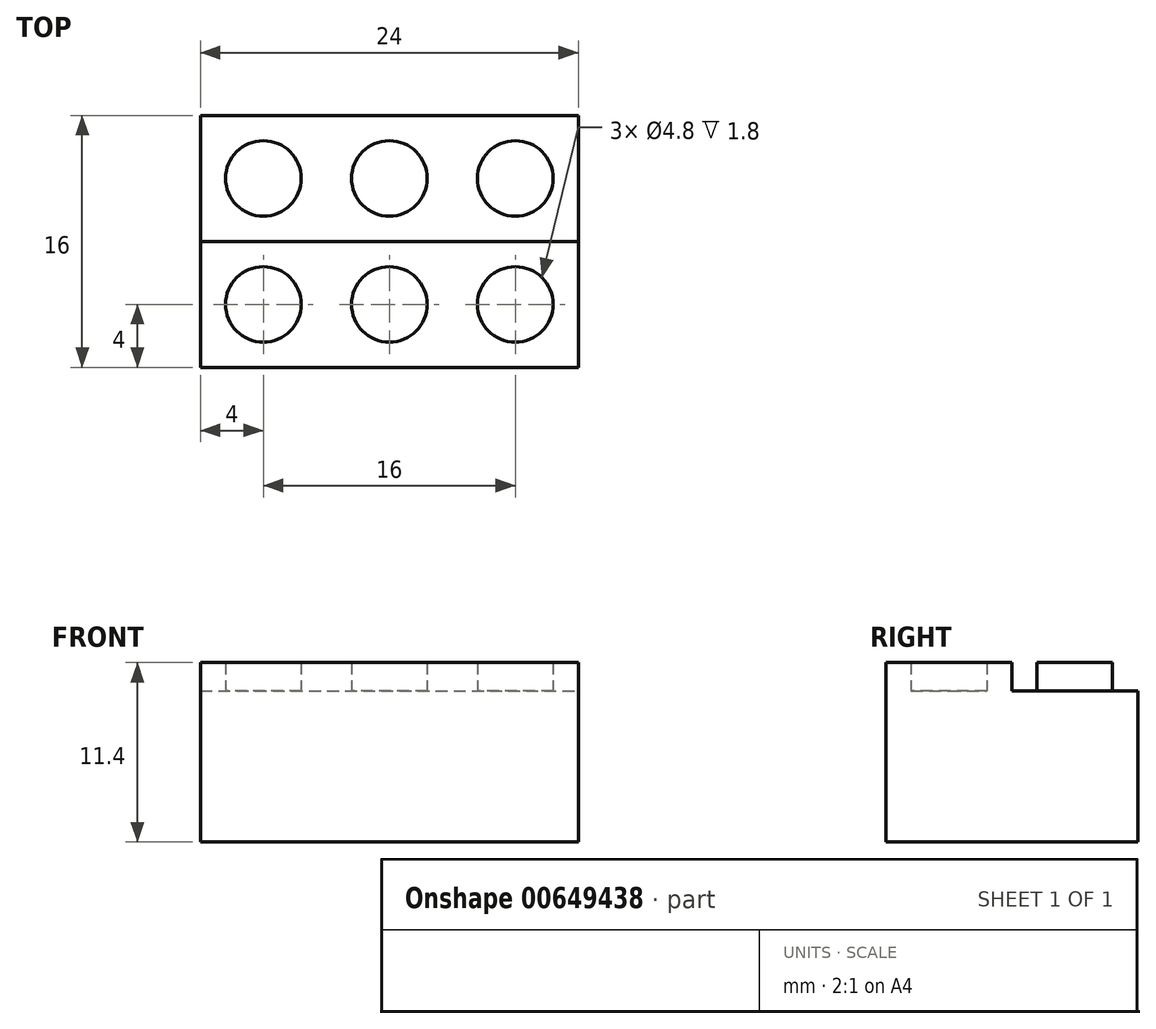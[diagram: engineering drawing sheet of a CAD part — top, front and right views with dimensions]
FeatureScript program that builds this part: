
annotation { "Feature Type Name" : "Feature", "Feature Type Description" : "" }
export const myFeature = defineFeature(function(context is Context, id is Id, definition is map)
    precondition{}
    {
        {
            var Q0;
            Q0=qCreatedBy(makeId("Top.planeOp"),FACE);
            var sketch = newSketch(context, id + "F0", { "sketchPlane" : qUnion([Q0])});
            skLineSegment(sketch, "E0.bottom", {"start": v(0, 0) * mm, "end": v(-24, 0) * mm});
            skLineSegment(sketch, "E0.top", {"start": v(0, 16) * mm, "end": v(-24, 16) * mm});
            skLineSegment(sketch, "E0.left", {"start": v(0, 0) * mm, "end": v(0, 16) * mm});
            skLineSegment(sketch, "E0.right", {"start": v(-24, 0) * mm, "end": v(-24, 16) * mm});
            skSolve(sketch);
        }
        {
            var Q0;
            Q0=makeQuery(id+"F0.imprint","IMPRINT",FACE,{"disambiguationData":[TD([[makeQuery(id+"F0.imprint","IMPRINT",EDGE,{"derivedFrom":sQuery(id+"F0.wireOp",EDGE,"E0.bottom")}),-1.0]])]});
            extrude(context, id + "F1", {"entities" : qUnion([Q0]), "depth" : 9.6 * mm, "offsetDistance" : 25.4 * mm});
        }
        {
            var Q0;
            Q0=makeQuery(id+"F1.opExtrude","CAP_FACE",FACE,{"disambiguationData":[OSD([sQuery(id+"F0.wireOp",EDGE,"E0.bottom"),sQuery(id+"F0.wireOp",EDGE,"E0.top"),sQuery(id+"F0.wireOp",EDGE,"E0.left"),sQuery(id+"F0.wireOp",EDGE,"E0.right")])],"isStart":false});
            var sketch = newSketch(context, id + "F2", { "sketchPlane" : qUnion([Q0])});
            skLineSegment(sketch, "E1", {"start": v(-24, 8) * mm, "end": v(0, 8) * mm});
            skLineSegment(sketch, "E2", {"start": v(-16, 16) * mm, "end": v(-16, 0) * mm});
            skLineSegment(sketch, "E3", {"start": v(-8, 16) * mm, "end": v(-8, 0) * mm});
            skCircle(sketch, "E4", {"center": v(-20, 12) * mm, "radius": 2.4 * mm});
            skCircle(sketch, "E5", {"center": v(-12, 12) * mm, "radius": 2.4 * mm});
            skCircle(sketch, "E6", {"center": v(-4, 12) * mm, "radius": 2.4 * mm});
            skCircle(sketch, "E7.MirrorC", {"center": v(-20, 4) * mm, "radius": 2.4 * mm});
            skCircle(sketch, "E8.MirrorC", {"center": v(-12, 4) * mm, "radius": 2.4 * mm});
            skCircle(sketch, "E9.MirrorC", {"center": v(-4, 4) * mm, "radius": 2.4 * mm});
            skSolve(sketch);
        }
        {
            var Q0;
            Q0=makeQuery(id+"F2.imprint","IMPRINT",FACE,{"disambiguationData":[TD([[makeQuery(id+"F2.imprint","IMPRINT",EDGE,{"derivedFrom":sQuery(id+"F2.wireOp",EDGE,"E4")}),1.0]])]});
            var Q1;
            Q1=makeQuery(id+"F2.imprint","IMPRINT",FACE,{"disambiguationData":[TD([[makeQuery(id+"F2.imprint","IMPRINT",EDGE,{"derivedFrom":sQuery(id+"F2.wireOp",EDGE,"E5")}),1.0]])]});
            var Q2;
            Q2=makeQuery(id+"F2.imprint","IMPRINT",FACE,{"disambiguationData":[TD([[makeQuery(id+"F2.imprint","IMPRINT",EDGE,{"derivedFrom":sQuery(id+"F2.wireOp",EDGE,"E6")}),1.0]])]});
            var Q3;
            Q3=makeQuery(id+"F2.imprint","IMPRINT",FACE,{"disambiguationData":[TD([[makeQuery(id+"F2.imprint","IMPRINT",EDGE,{"derivedFrom":sQuery(id+"F2.wireOp",EDGE,"E9.MirrorC")}),-1.0]])]});
            var Q4;
            Q4=makeQuery(id+"F2.imprint","IMPRINT",FACE,{"disambiguationData":[TD([[makeQuery(id+"F2.imprint","IMPRINT",EDGE,{"derivedFrom":sQuery(id+"F2.wireOp",EDGE,"E8.MirrorC")}),-1.0]])]});
            var Q5;
            Q5=makeQuery(id+"F2.imprint","IMPRINT",FACE,{"disambiguationData":[TD([[makeQuery(id+"F2.imprint","IMPRINT",EDGE,{"derivedFrom":sQuery(id+"F2.wireOp",EDGE,"E7.MirrorC")}),-1.0]])]});
            extrude(context, id + "F3", {"entities" : qUnion([Q0, Q1, Q2, Q3, Q4, Q5]), "operationType" : NewBodyOperationType.ADD, "depth" : 1.8 * mm, "offsetDistance" : 25.4 * mm});
        }
    });
